# Revit family: 304_Cim717PHF-_
name_source: partatom
category: Pipe Accessories
units: mm (PartAtom-declared; Revit-internal decimal feet)

## family parameters
Always vertical = Yes
Cut with Voids When Loaded = No
Part Type = Valve - Breaks Into
Round Connector Dimension = Use Diameter
Shared = No
Work Plane-Based = No

## types (4) — shared parameters
A = 35 mm  [stored 0.114829 ft]
A1 = 32 mm  [stored 0.104987 ft]
CAT0 = Yes
CH = 20 mm  [stored 0.0656168 ft]
D2 = 16 mm  [stored 0.0524934 ft]
Description = AUTOMATIC BALANCING VALVE P.I.C.V. - PN 25 - "CR" BRASS - HIGH FLOW
H1 = 25 mm  [stored 0.082021 ft]
H2 = 14 mm  [stored 0.0459318 ft]
L2D_Min = 3048 mm  [stored 10 ft]
Manufacturer = Cimberio
QmdConnectorList = 301;D;302;D
URL = www.cimberio.it
magiPartTypeId = 304
magiProductFamilyId = Cim717PHF-*
zero-valued in all types: MC_Default_elevation

## per-type parameters (varying)
| type | D | D1 | H3 | H4 | H4__ve | L | L2 | L2D | LL | T | W2D |
| Cim717PHF-10 | 15 mm | 20 mm  [stored 0.0656168 ft] | 36 mm  [stored 0.11811 ft] | 55 mm  [stored 0.180446 ft] | -55 mm  [stored -0.180446 ft] | 53 mm  [stored 0.173885 ft] | 10 mm  [stored 0.0328084 ft] | 53 mm  [stored 0.173885 ft] | 27 mm | 15 mm  [stored 0.0492126 ft] | 15 mm  [stored 0.0492126 ft] |
| Cim717PHF-25 | 32 mm | 42 mm | 44 mm  [stored 0.144357 ft] | 63 mm  [stored 0.206693 ft] | -63 mm  [stored -0.206693 ft] | 104 mm  [stored 0.341207 ft] | 15 mm  [stored 0.0492126 ft] | 104 mm  [stored 0.341207 ft] | 52 mm  [stored 0.170604 ft] | 32 mm  [stored 0.104987 ft] | 32 mm  [stored 0.104987 ft] |
| Cim717PHF-20 | 25 mm | 33 mm | 46 mm  [stored 0.150919 ft] | 65 mm  [stored 0.213255 ft] | -65 mm  [stored -0.213255 ft] | 82 mm  [stored 0.269029 ft] | 15 mm  [stored 0.0492126 ft] | 82 mm  [stored 0.269029 ft] | 41 mm  [stored 0.134514 ft] | 25 mm  [stored 0.082021 ft] | 25 mm  [stored 0.082021 ft] |
| Cim717PHF-15 | 20 mm | 26 mm  [stored 0.0853018 ft] | 36 mm  [stored 0.11811 ft] | 55 mm  [stored 0.180446 ft] | -55 mm  [stored -0.180446 ft] | 65 mm  [stored 0.213255 ft] | 15 mm  [stored 0.0492126 ft] | 65 mm  [stored 0.213255 ft] | 33 mm | 20 mm  [stored 0.0656168 ft] | 20 mm  [stored 0.0656168 ft] |

note: column(s) folded — value = type name in every type: magiProductCode, magiProductId

note: [stored X ft] marks values corroborated as IEEE doubles in the binary element streams (Revit-internal decimal feet)

## geometry (parser evidence)
native form markers: Sweep x2
no freeform markers — native parametric forms only
